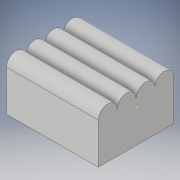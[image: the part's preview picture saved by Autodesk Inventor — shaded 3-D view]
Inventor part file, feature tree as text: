
AUTODESK INVENTOR PART (.ipt)
format: ipt  version: 2018 (Build 220112000, 112)  size: 119,808 bytes
history: native  units: in
note: dims shown in document units (in); Inventor stores cm internally (conversion verified against a paired STEP export)
features: sketch x4, extrude x2
ambient origin geometry x8: Origin, YZ Plane, XZ Plane, XY Plane, X Axis, Y Axis, Z Axis, Center Point
bodies: Solid1 (feature_tree)
feature tree (6):
  sketch  "Sketch1"  dims[d0=1.7717in d1=1.1811in]
  extrude  "Extrusion1"  Depth=1.7717in
  sketch  "Sketch3"  dims[d5=0.4429in]
  extrude  "Extrusion2"  Depth=2.1654in
  sketch  "Sketch2"  dims[d2=2.1654in d3=0.0in d4=0.4429in]
  sketch  "Sketch4"  dims[d6=0.4429in d7=0.4429in d8=2.3622in d9=0.0in]
